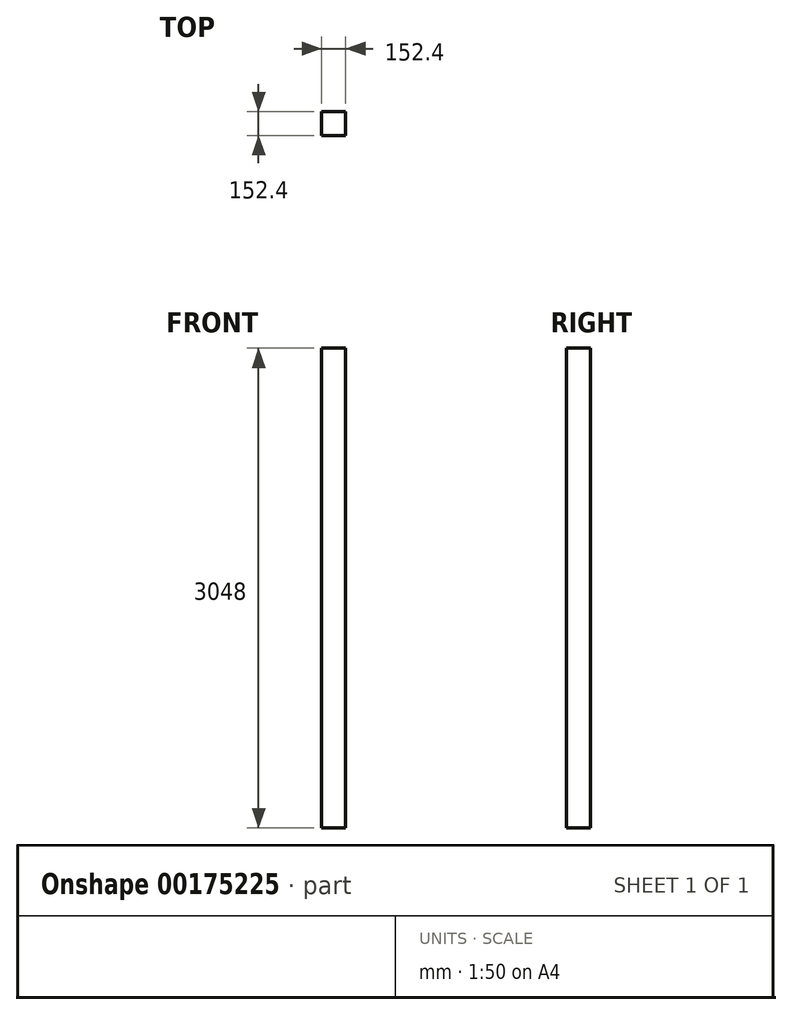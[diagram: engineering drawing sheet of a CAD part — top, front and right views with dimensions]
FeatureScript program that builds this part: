
annotation { "Feature Type Name" : "Feature", "Feature Type Description" : "" }
export const myFeature = defineFeature(function(context is Context, id is Id, definition is map)
    precondition{}
    {
        {
            var Q0;
            Q0=qCreatedBy(makeId("Top.planeOp"),FACE);
            var sketch = newSketch(context, id + "F0", { "sketchPlane" : qUnion([Q0])});
            skLineSegment(sketch, "E0.bottom", {"start": v(76.2, 76.2) * mm, "end": v(-76.2, 76.2) * mm});
            skLineSegment(sketch, "E0.top", {"start": v(76.2, -76.2) * mm, "end": v(-76.2, -76.2) * mm});
            skLineSegment(sketch, "E0.left", {"start": v(76.2, 76.2) * mm, "end": v(76.2, -76.2) * mm});
            skLineSegment(sketch, "E0.right", {"start": v(-76.2, 76.2) * mm, "end": v(-76.2, -76.2) * mm});
            skPoint(sketch, "E0.middle", {"position": v(0, 0) * mm});
            skSolve(sketch);
        }
        {
            var Q0;
            Q0 = qSketchRegion(id + "F0", true);
            extrude(context, id + "F1", {"entities" : qUnion([Q0]), "depth" : 3048 * mm});
        }
    });
